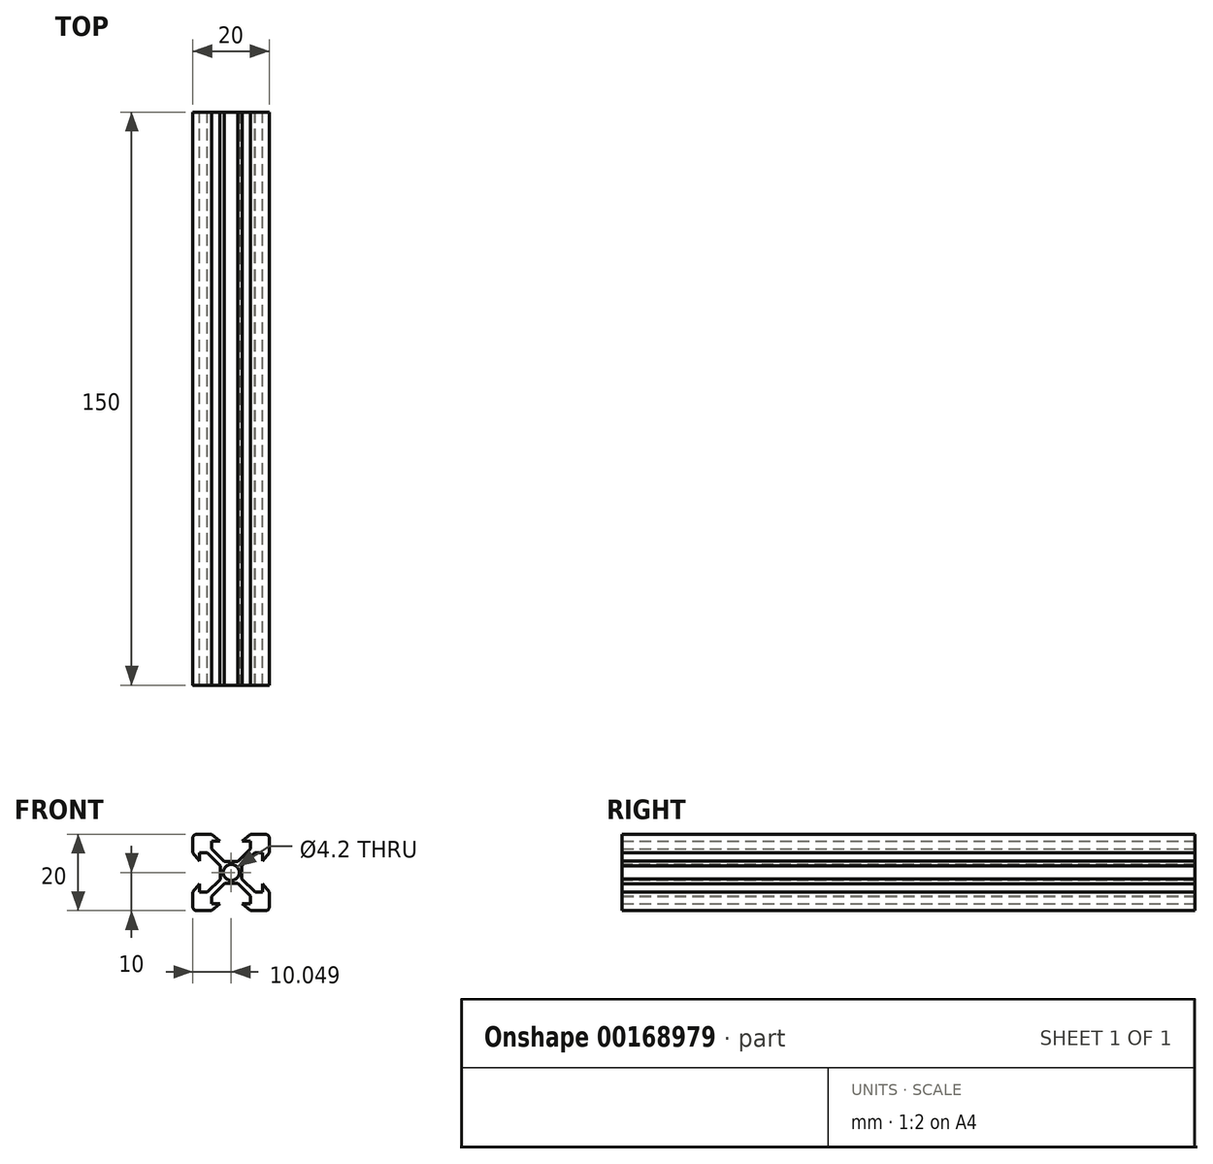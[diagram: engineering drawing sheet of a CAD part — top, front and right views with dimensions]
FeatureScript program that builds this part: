
annotation { "Feature Type Name" : "Feature", "Feature Type Description" : "" }
export const myFeature = defineFeature(function(context is Context, id is Id, definition is map)
    precondition{}
    {
        {
            var Q0;
            Q0=qCreatedBy(makeId("Front.planeOp"),FACE);
            var sketch = newSketch(context, id + "F0", { "sketchPlane" : qUnion([Q0])});
            skLineSegment(sketch, "E0.left", {"start": v(15, 1) * mm, "end": v(15, 4.89) * mm});
            skLineSegment(sketch, "E0.right", {"start": v(35, 1) * mm, "end": v(35, 4.89) * mm});
            skLineSegment(sketch, "E1.right", {"start": v(33.2, 2.97) * mm, "end": v(33.2, 7.06) * mm});
            skLineSegment(sketch, "E2.rect.bottom", {"start": v(26.78, 12.84) * mm, "end": v(23.22, 12.84) * mm});
            skLineSegment(sketch, "E2.rect.top", {"start": v(26.78, 7.16) * mm, "end": v(23.31, 7.16) * mm});
            skLineSegment(sketch, "E2.rect.left", {"start": v(27.84, 11.78) * mm, "end": v(27.84, 8.33) * mm});
            skLineSegment(sketch, "E2.rect.right", {"start": v(22.16, 11.78) * mm, "end": v(22.16, 8.22) * mm});
            skLineSegment(sketch, "E3.rect.bottom", {"start": v(35, 15.12) * mm, "end": v(35, 15.12) * mm});
            skLineSegment(sketch, "E4.rect.bottom", {"start": v(33.2, 12.95) * mm, "end": v(33.2, 12.95) * mm});
            skPoint(sketch, "E4.rect.middle", {"position": v(33.2, 10) * mm});
            skLineSegment(sketch, "E5", {"start": v(35, 4.88) * mm, "end": v(33.2, 7.05) * mm});
            skLineSegment(sketch, "E6", {"start": v(28.37, 12.3) * mm, "end": v(33.2, 17.14) * mm});
            skLineSegment(sketch, "E7", {"start": v(27.3, 13.37) * mm, "end": v(32.14, 18.2) * mm});
            skLineSegment(sketch, "E8", {"start": v(22.7, 13.37) * mm, "end": v(17.86, 18.2) * mm});
            skLineSegment(sketch, "E9", {"start": v(28.37, 7.8) * mm, "end": v(33.2, 2.97) * mm});
            skLineSegment(sketch, "E10", {"start": v(22.74, 6.58) * mm, "end": v(17.95, 1.8) * mm});
            skLineSegment(sketch, "E11", {"start": v(27.36, 6.58) * mm, "end": v(32.14, 1.8) * mm});
            skLineSegment(sketch, "E12", {"start": v(21.63, 7.7) * mm, "end": v(16.8, 2.86) * mm});
            skLineSegment(sketch, "E13", {"start": v(22.7, 13.37) * mm, "end": v(23.22, 12.84) * mm});
            skLineSegment(sketch, "E14", {"start": v(27.3, 13.37) * mm, "end": v(26.78, 12.84) * mm});
            skLineSegment(sketch, "E15", {"start": v(28.37, 12.3) * mm, "end": v(27.84, 11.78) * mm});
            skLineSegment(sketch, "E16", {"start": v(28.37, 7.8) * mm, "end": v(27.84, 8.33) * mm});
            skLineSegment(sketch, "E17", {"start": v(27.36, 6.58) * mm, "end": v(26.78, 7.16) * mm});
            skLineSegment(sketch, "E18", {"start": v(22.74, 6.58) * mm, "end": v(23.31, 7.16) * mm});
            skLineSegment(sketch, "E19", {"start": v(21.63, 7.7) * mm, "end": v(22.16, 8.22) * mm});
            skLineSegment(sketch, "E20", {"start": v(21.63, 12.3) * mm, "end": v(16.8, 17.14) * mm});
            skLineSegment(sketch, "E21", {"start": v(21.63, 12.3) * mm, "end": v(22.16, 11.78) * mm});
            skPoint(sketch, "E22.orphan", {"position": v(22.16, 12.84) * mm});
            skPoint(sketch, "E23.orphan", {"position": v(27.84, 12.84) * mm});
            skPoint(sketch, "E24.orphan", {"position": v(27.84, 7.16) * mm});
            skPoint(sketch, "E25.orphan", {"position": v(22.16, 7.16) * mm});
            skPoint(sketch, "E26.orphan", {"position": v(33.2, 18.2) * mm});
            skPoint(sketch, "E27.orphan", {"position": v(33.2, 1.8) * mm});
            skLineSegment(sketch, "E28.trimOffspring", {"start": v(35, 15.12) * mm, "end": v(35, 19) * mm});
            skLineSegment(sketch, "E29.rect.left", {"start": v(28.21, 18.2) * mm, "end": v(28.21, 18.2) * mm});
            skLineSegment(sketch, "E29.rect.right", {"start": v(21.79, 18.2) * mm, "end": v(21.79, 18.2) * mm});
            skLineSegment(sketch, "E30.rect.left", {"start": v(27.72, 16.15) * mm, "end": v(27.72, 16.15) * mm});
            skLineSegment(sketch, "E30.rect.right", {"start": v(21.83, 16.15) * mm, "end": v(21.83, 16.15) * mm});
            skLineSegment(sketch, "E31.trimOffspring", {"start": v(15, 15.12) * mm, "end": v(15, 19) * mm});
            skPoint(sketch, "E32.visualSharp", {"position": v(15, 20) * mm});
            skArc(sketch, "E32.filletArc", {"start": v(16, 20) * mm, "mid": v(15.3, 19.7) * mm, "end": v(15, 19) * mm});
            skArc(sketch, "E33.filletArc", {"start": v(34, 0) * mm, "mid": v(34.7, 0.3) * mm, "end": v(35, 1) * mm});
            skPoint(sketch, "E34.visualSharp", {"position": v(35, 20) * mm});
            skArc(sketch, "E34.filletArc", {"start": v(35, 19) * mm, "mid": v(34.7, 19.7) * mm, "end": v(34, 20) * mm});
            skLineSegment(sketch, "E35", {"start": v(17.95, 1.8) * mm, "end": v(17.95, 0) * mm});
            skArc(sketch, "E36.filletArc", {"start": v(15, 1) * mm, "mid": v(15.3, 0.3) * mm, "end": v(16, 0) * mm});
            skLineSegment(sketch, "E37", {"start": v(16.8, 17.14) * mm, "end": v(17.86, 18.2) * mm});
            skPoint(sketch, "E38.visualSharp", {"position": v(16.8, 12.95) * mm});
            skLineSegment(sketch, "E39", {"start": v(16.8, 2.86) * mm, "end": v(17.95, 1.8) * mm});
            skLineSegment(sketch, "E40", {"start": v(32.14, 1.8) * mm, "end": v(33.2, 2.97) * mm});
            skLineSegment(sketch, "E41", {"start": v(32.14, 18.2) * mm, "end": v(33.2, 17.14) * mm});
            skLineSegment(sketch, "E42", {"start": v(33.2, 17.14) * mm, "end": v(33.2, 12.94) * mm});
            skLineSegment(sketch, "E43", {"start": v(35, 15.12) * mm, "end": v(33.2, 12.95) * mm});
            skPoint(sketch, "E44.visualSharp", {"position": v(16.8, 7.06) * mm});
            skLineSegment(sketch, "E45", {"start": v(33.2, 15.12) * mm, "end": v(31.18, 15.12) * mm});
            skLineSegment(sketch, "E46", {"start": v(16.8, 15.12) * mm, "end": v(18.82, 15.12) * mm});
            skLineSegment(sketch, "E47", {"start": v(16.8, 4.89) * mm, "end": v(18.82, 4.89) * mm});
            skLineSegment(sketch, "E48", {"start": v(33.2, 4.89) * mm, "end": v(31.28, 4.88) * mm});
            skLineSegment(sketch, "E49.rect.left", {"start": v(26.7, 18.2) * mm, "end": v(26.7, 18.2) * mm});
            skLineSegment(sketch, "E49.rect.right", {"start": v(23.3, 18.2) * mm, "end": v(23.3, 18.2) * mm});
            skPoint(sketch, "E49.rect.middle", {"position": v(25, 18.2) * mm});
            skLineSegment(sketch, "E50.rect.left", {"start": v(30.11, 20) * mm, "end": v(30.11, 20) * mm});
            skLineSegment(sketch, "E50.rect.right", {"start": v(19.88, 20) * mm, "end": v(19.88, 20) * mm});
            skPoint(sketch, "E50.rect.middle", {"position": v(25, 20) * mm});
            skLineSegment(sketch, "E51.rect.left", {"start": v(27.95, 18.2) * mm, "end": v(27.95, 18.2) * mm});
            skLineSegment(sketch, "E51.rect.right", {"start": v(22.05, 18.2) * mm, "end": v(22.05, 18.2) * mm});
            skLineSegment(sketch, "E52", {"start": v(22.05, 18.2) * mm, "end": v(19.88, 20) * mm});
            skLineSegment(sketch, "E53", {"start": v(27.94, 18.2) * mm, "end": v(30.11, 20) * mm});
            skLineSegment(sketch, "E54", {"start": v(27.94, 18.2) * mm, "end": v(32.14, 18.2) * mm});
            skLineSegment(sketch, "E55", {"start": v(30.11, 20) * mm, "end": v(34, 20) * mm});
            skLineSegment(sketch, "E56", {"start": v(19.88, 20) * mm, "end": v(16, 20) * mm});
            skLineSegment(sketch, "E57", {"start": v(17.86, 18.2) * mm, "end": v(22.05, 18.2) * mm});
            skLineSegment(sketch, "E58", {"start": v(15, 15.11) * mm, "end": v(16.8, 12.94) * mm});
            skLineSegment(sketch, "E59", {"start": v(16.8, 17.14) * mm, "end": v(16.8, 12.95) * mm});
            skLineSegment(sketch, "E60", {"start": v(15, 4.89) * mm, "end": v(16.8, 7.06) * mm});
            skLineSegment(sketch, "E61", {"start": v(16.8, 2.86) * mm, "end": v(16.8, 7.06) * mm});
            skLineSegment(sketch, "E62", {"start": v(22.05, 1.8) * mm, "end": v(19.88, 0) * mm});
            skLineSegment(sketch, "E63", {"start": v(27.94, 1.8) * mm, "end": v(30.11, 0) * mm});
            skLineSegment(sketch, "E64", {"start": v(16, 0) * mm, "end": v(19.88, 0) * mm});
            skLineSegment(sketch, "E65", {"start": v(30.11, 0) * mm, "end": v(34, 0) * mm});
            skLineSegment(sketch, "E66", {"start": v(27.94, 1.8) * mm, "end": v(32.14, 1.8) * mm});
            skLineSegment(sketch, "E67", {"start": v(22.05, 1.8) * mm, "end": v(17.95, 1.8) * mm});
            skLineSegment(sketch, "E68", {"start": v(19.88, 1.8) * mm, "end": v(19.88, 3.73) * mm});
            skLineSegment(sketch, "E69", {"start": v(30.11, 1.8) * mm, "end": v(30.11, 3.83) * mm});
            skLineSegment(sketch, "E70", {"start": v(30.11, 18.2) * mm, "end": v(30.11, 16.18) * mm});
            skLineSegment(sketch, "E71", {"start": v(19.88, 16.18) * mm, "end": v(19.88, 18.2) * mm});
            skLineSegment(sketch, "E72", {"start": v(15, 0) * mm, "end": v(-35, 0) * mm});
            skLineSegment(sketch, "E73", {"start": v(35, 0) * mm, "end": v(35, 20) * mm});
            skLineSegment(sketch, "E74", {"start": v(34, 0) * mm, "end": v(35, 0) * mm});
            skLineSegment(sketch, "E75", {"start": v(34, 20) * mm, "end": v(35, 20) * mm});
            skLineSegment(sketch, "E76.0.MirrorCS", {"start": v(36, 0) * mm, "end": v(35, 0) * mm});
            skArc(sketch, "E76.1.MirrorCS", {"start": v(36, 0) * mm, "mid": v(35.3, 0.3) * mm, "end": v(35, 1) * mm});
            skLineSegment(sketch, "E76.2.MirrorCS", {"start": v(36, 20) * mm, "end": v(35, 20) * mm});
            skLineSegment(sketch, "E76.3.MirrorCS", {"start": v(54, 0) * mm, "end": v(50.12, 0) * mm});
            skLineSegment(sketch, "E76.4.MirrorCS", {"start": v(48.37, 7.7) * mm, "end": v(47.84, 8.22) * mm});
            skArc(sketch, "E76.5.MirrorCS", {"start": v(35, 19) * mm, "mid": v(35.3, 19.7) * mm, "end": v(36, 20) * mm});
            skLineSegment(sketch, "E76.6.MirrorCS", {"start": v(37.86, 1.8) * mm, "end": v(36.8, 2.97) * mm});
            skArc(sketch, "E76.7.MirrorCS", {"start": v(54, 20) * mm, "mid": v(54.7, 19.7) * mm, "end": v(55, 19) * mm});
            skLineSegment(sketch, "E76.8.MirrorCS", {"start": v(42.64, 6.58) * mm, "end": v(43.22, 7.16) * mm});
            skLineSegment(sketch, "E76.9.MirrorCS", {"start": v(41.63, 7.8) * mm, "end": v(42.16, 8.33) * mm});
            skLineSegment(sketch, "E76.10.MirrorCS", {"start": v(37.86, 18.2) * mm, "end": v(36.8, 17.14) * mm});
            skLineSegment(sketch, "E76.11.MirrorCS", {"start": v(42.7, 13.37) * mm, "end": v(43.22, 12.84) * mm});
            skLineSegment(sketch, "E76.12.MirrorCS", {"start": v(53.2, 2.86) * mm, "end": v(52.05, 1.8) * mm});
            skLineSegment(sketch, "E76.13.MirrorCS", {"start": v(53.2, 17.14) * mm, "end": v(52.14, 18.2) * mm});
            skLineSegment(sketch, "E76.14.MirrorCS", {"start": v(48.37, 12.3) * mm, "end": v(47.84, 11.78) * mm});
            skLineSegment(sketch, "E76.15.MirrorCS", {"start": v(47.3, 13.37) * mm, "end": v(46.78, 12.84) * mm});
            skLineSegment(sketch, "E76.16.MirrorCS", {"start": v(47.26, 6.58) * mm, "end": v(46.69, 7.16) * mm});
            skLineSegment(sketch, "E76.17.MirrorCS", {"start": v(36.8, 15.12) * mm, "end": v(38.82, 15.12) * mm});
            skLineSegment(sketch, "E76.19.MirrorCS", {"start": v(54, 0) * mm, "end": v(50.12, 0) * mm});
            skLineSegment(sketch, "E76.20.MirrorCS", {"start": v(36.8, 4.89) * mm, "end": v(38.72, 4.88) * mm});
            skArc(sketch, "E76.21.MirrorCS", {"start": v(55, 1) * mm, "mid": v(54.7, 0.3) * mm, "end": v(54, 0) * mm});
            skLineSegment(sketch, "E76.22.MirrorCS", {"start": v(55, 4.89) * mm, "end": v(53.2, 7.06) * mm});
            skLineSegment(sketch, "E76.23.MirrorCS", {"start": v(52.14, 18.2) * mm, "end": v(47.95, 18.2) * mm});
            skLineSegment(sketch, "E76.25.MirrorCS", {"start": v(47.95, 18.2) * mm, "end": v(50.12, 20) * mm});
            skLineSegment(sketch, "E76.26.MirrorCS", {"start": v(50.12, 1.8) * mm, "end": v(50.12, 3.73) * mm});
            skLineSegment(sketch, "E76.27.MirrorCS", {"start": v(39.89, 0) * mm, "end": v(36, 0) * mm});
            skLineSegment(sketch, "E76.28.MirrorCS", {"start": v(53.2, 15.12) * mm, "end": v(51.18, 15.12) * mm});
            skPoint(sketch, "E76.29.MirrorP", {"position": v(45, 18.2) * mm});
            skLineSegment(sketch, "E76.30.MirrorCS", {"start": v(48.21, 18.2) * mm, "end": v(48.21, 18.2) * mm});
            skLineSegment(sketch, "E76.31.MirrorCS", {"start": v(42.06, 18.2) * mm, "end": v(39.89, 20) * mm});
            skLineSegment(sketch, "E76.32.MirrorCS", {"start": v(41.63, 12.3) * mm, "end": v(42.16, 11.78) * mm});
            skLineSegment(sketch, "E76.33.MirrorCS", {"start": v(41.79, 18.2) * mm, "end": v(41.79, 18.2) * mm});
            skLineSegment(sketch, "E76.34.MirrorCS", {"start": v(36.8, 17.14) * mm, "end": v(36.8, 12.94) * mm});
            skLineSegment(sketch, "E76.35.MirrorCS", {"start": v(50.12, 16.18) * mm, "end": v(50.12, 18.2) * mm});
            skLineSegment(sketch, "E76.36.MirrorCS", {"start": v(42.06, 1.8) * mm, "end": v(39.89, 0) * mm});
            skLineSegment(sketch, "E76.37.MirrorCS", {"start": v(35, 15.12) * mm, "end": v(36.8, 12.95) * mm});
            skLineSegment(sketch, "E76.38.MirrorCS", {"start": v(35, 4.88) * mm, "end": v(36.8, 7.05) * mm});
            skLineSegment(sketch, "E76.39.MirrorCS", {"start": v(53.2, 17.14) * mm, "end": v(53.2, 12.95) * mm});
            skLineSegment(sketch, "E76.40.MirrorCS", {"start": v(55, 15.12) * mm, "end": v(53.2, 12.94) * mm});
            skLineSegment(sketch, "E76.41.MirrorCS", {"start": v(53.2, 4.89) * mm, "end": v(51.18, 4.89) * mm});
            skLineSegment(sketch, "E76.42.MirrorCS", {"start": v(36.8, 2.97) * mm, "end": v(36.8, 7.06) * mm});
            skLineSegment(sketch, "E76.43.MirrorCS", {"start": v(39.89, 18.2) * mm, "end": v(39.89, 16.18) * mm});
            skLineSegment(sketch, "E76.44.MirrorCS", {"start": v(42.06, 18.2) * mm, "end": v(37.86, 18.2) * mm});
            skLineSegment(sketch, "E76.45.MirrorCS", {"start": v(53.2, 2.86) * mm, "end": v(53.2, 7.06) * mm});
            skLineSegment(sketch, "E76.46.MirrorCS", {"start": v(42.06, 1.8) * mm, "end": v(37.86, 1.8) * mm});
            skLineSegment(sketch, "E76.47.MirrorCS", {"start": v(52.05, 1.8) * mm, "end": v(52.05, 0) * mm});
            skLineSegment(sketch, "E76.48.MirrorCS", {"start": v(39.89, 1.8) * mm, "end": v(39.89, 3.83) * mm});
            skPoint(sketch, "E76.49.MirrorP", {"position": v(55, 20) * mm});
            skLineSegment(sketch, "E76.50.MirrorCS", {"start": v(47.95, 1.8) * mm, "end": v(52.05, 1.8) * mm});
            skLineSegment(sketch, "E76.51.MirrorCS", {"start": v(41.63, 7.8) * mm, "end": v(36.8, 2.97) * mm});
            skPoint(sketch, "E76.52.MirrorP", {"position": v(53.2, 7.06) * mm});
            skLineSegment(sketch, "E76.53.MirrorCS", {"start": v(43.22, 7.16) * mm, "end": v(46.69, 7.16) * mm});
            skLineSegment(sketch, "E76.54.MirrorCS", {"start": v(55, 1) * mm, "end": v(55, 4.89) * mm});
            skLineSegment(sketch, "E76.55.MirrorCS", {"start": v(55, 15.12) * mm, "end": v(55, 19) * mm});
            skLineSegment(sketch, "E76.56.MirrorCS", {"start": v(48.37, 12.3) * mm, "end": v(53.2, 17.14) * mm});
            skLineSegment(sketch, "E76.57.MirrorCS", {"start": v(42.28, 16.15) * mm, "end": v(42.28, 16.15) * mm});
            skLineSegment(sketch, "E76.58.MirrorCS", {"start": v(36.8, 12.95) * mm, "end": v(36.8, 12.95) * mm});
            skLineSegment(sketch, "E76.60.MirrorCS", {"start": v(42.05, 18.2) * mm, "end": v(42.05, 18.2) * mm});
            skLineSegment(sketch, "E76.61.MirrorCS", {"start": v(47.26, 6.58) * mm, "end": v(52.05, 1.8) * mm});
            skLineSegment(sketch, "E76.62.MirrorCS", {"start": v(42.7, 13.37) * mm, "end": v(37.86, 18.2) * mm});
            skPoint(sketch, "E76.63.MirrorP", {"position": v(42.16, 12.84) * mm});
            skLineSegment(sketch, "E76.64.MirrorCS", {"start": v(48.17, 16.15) * mm, "end": v(48.17, 16.15) * mm});
            skLineSegment(sketch, "E76.65.MirrorCS", {"start": v(42.16, 11.78) * mm, "end": v(42.16, 8.33) * mm});
            skLineSegment(sketch, "E76.66.MirrorCS", {"start": v(47.84, 11.78) * mm, "end": v(47.84, 8.22) * mm});
            skLineSegment(sketch, "E76.67.MirrorCS", {"start": v(43.22, 12.84) * mm, "end": v(46.78, 12.84) * mm});
            skPoint(sketch, "E76.68.MirrorP", {"position": v(36.8, 18.2) * mm});
            skPoint(sketch, "E76.69.MirrorP", {"position": v(53.2, 12.95) * mm});
            skLineSegment(sketch, "E76.72.MirrorCS", {"start": v(39.89, 20) * mm, "end": v(36, 20) * mm});
            skPoint(sketch, "E76.73.MirrorP", {"position": v(42.16, 7.16) * mm});
            skLineSegment(sketch, "E76.74.MirrorCS", {"start": v(47.3, 13.37) * mm, "end": v(52.14, 18.2) * mm});
            skLineSegment(sketch, "E76.75.MirrorCS", {"start": v(43.3, 18.2) * mm, "end": v(43.3, 18.2) * mm});
            skLineSegment(sketch, "E76.76.MirrorCS", {"start": v(39.89, 0) * mm, "end": v(36, 0) * mm});
            skLineSegment(sketch, "E76.77.MirrorCS", {"start": v(54, 0) * mm, "end": v(50.12, 0) * mm});
            skLineSegment(sketch, "E76.78.MirrorCS", {"start": v(39.89, 0) * mm, "end": v(36, 0) * mm});
            skPoint(sketch, "E76.79.MirrorP", {"position": v(45, 20) * mm});
            skPoint(sketch, "E76.80.MirrorP", {"position": v(47.84, 7.16) * mm});
            skLineSegment(sketch, "E76.81.MirrorCS", {"start": v(39.89, 20) * mm, "end": v(39.89, 20) * mm});
            skLineSegment(sketch, "E76.82.MirrorCS", {"start": v(47.95, 18.2) * mm, "end": v(47.95, 18.2) * mm});
            skLineSegment(sketch, "E76.83.MirrorCS", {"start": v(50.12, 20) * mm, "end": v(50.12, 20) * mm});
            skLineSegment(sketch, "E76.84.MirrorCS", {"start": v(41.63, 12.3) * mm, "end": v(36.8, 17.14) * mm});
            skLineSegment(sketch, "E76.85.MirrorCS", {"start": v(48.37, 7.7) * mm, "end": v(53.2, 2.86) * mm});
            skPoint(sketch, "E76.86.MirrorP", {"position": v(36.8, 1.8) * mm});
            skPoint(sketch, "E76.87.MirrorP", {"position": v(36.8, 10) * mm});
            skPoint(sketch, "E76.88.MirrorP", {"position": v(45, 18.2) * mm});
            skPoint(sketch, "E76.89.MirrorP", {"position": v(47.84, 12.84) * mm});
            skLineSegment(sketch, "E76.90.MirrorCS", {"start": v(47.95, 1.8) * mm, "end": v(50.12, 0) * mm});
            skLineSegment(sketch, "E76.91.MirrorCS", {"start": v(42.64, 6.58) * mm, "end": v(37.86, 1.8) * mm});
            skLineSegment(sketch, "E76.94.MirrorCS", {"start": v(50.12, 20) * mm, "end": v(54, 20) * mm});
            skLineSegment(sketch, "E76.95.MirrorCS", {"start": v(46.7, 18.2) * mm, "end": v(46.7, 18.2) * mm});
            skSolve(sketch);
        }
        {
            var Q0;
            Q0=makeQuery(id+"F0.imprint","IMPRINT",FACE,{"disambiguationData":[TD([[makeQuery(id+"F0.imprint","IMPRINT",EDGE,{"derivedFrom":sQuery(id+"F0.wireOp",EDGE,"E2.rect.bottom")}),1.0]])]});
            var Q1;
            {var subQ3=sQuery(id+"F0.wireOp",EDGE,"E69");Q1=makeQuery(id+"F0.imprint","IMPRINT",FACE,{"disambiguationData":[TD([[makeQuery(id+"F0.imprint","IMPRINT",EDGE,{"derivedFrom":subQ3}),-1.0]])]});}
            var Q2;
            {var subQ3=sQuery(id+"F0.wireOp",EDGE,"E47");Q2=makeQuery(id+"F0.imprint","IMPRINT",FACE,{"disambiguationData":[TD([[makeQuery(id+"F0.imprint","IMPRINT",EDGE,{"derivedFrom":subQ3}),-1.0]])]});}
            var Q3;
            Q3=makeQuery(id+"F0.imprint","IMPRINT",FACE,{"disambiguationData":[TD([[makeQuery(id+"F0.imprint","IMPRINT",EDGE,{"derivedFrom":sQuery(id+"F0.wireOp",EDGE,"E0.left")}),-1.0]])]});
            var Q4;
            {var subQ1=sQuery(id+"F0.wireOp",EDGE,"E35");Q4=makeQuery(id+"F0.imprint","IMPRINT",FACE,{"disambiguationData":[TD([[makeQuery(id+"F0.imprint","IMPRINT",EDGE,{"derivedFrom":subQ1}),1.0]])]});}
            var Q5;
            Q5=makeQuery(id+"F0.imprint","IMPRINT",FACE,{"disambiguationData":[TD([[makeQuery(id+"F0.imprint","IMPRINT",EDGE,{"derivedFrom":sQuery(id+"F0.wireOp",EDGE,"E31.trimOffspring")}),-1.0]])]});
            var Q6;
            {var subQ3=sQuery(id+"F0.wireOp",EDGE,"E71");Q6=makeQuery(id+"F0.imprint","IMPRINT",FACE,{"disambiguationData":[TD([[makeQuery(id+"F0.imprint","IMPRINT",EDGE,{"derivedFrom":subQ3}),1.0]])]});}
            var Q7;
            Q7=makeQuery(id+"F0.imprint","IMPRINT",FACE,{"disambiguationData":[TD([[makeQuery(id+"F0.imprint","IMPRINT",EDGE,{"derivedFrom":sQuery(id+"F0.wireOp",EDGE,"E34.filletArc")}),1.0]])]});
            var Q8;
            {var subQ3=sQuery(id+"F0.wireOp",EDGE,"E45");Q8=makeQuery(id+"F0.imprint","IMPRINT",FACE,{"disambiguationData":[TD([[makeQuery(id+"F0.imprint","IMPRINT",EDGE,{"derivedFrom":subQ3}),-1.0]])]});}
            var Q9;
            {var subQ3=sQuery(id+"F0.wireOp",EDGE,"E48");Q9=makeQuery(id+"F0.imprint","IMPRINT",FACE,{"disambiguationData":[TD([[makeQuery(id+"F0.imprint","IMPRINT",EDGE,{"derivedFrom":subQ3}),1.0]])]});}
            var Q10;
            {var subQ3=sQuery(id+"F0.wireOp",EDGE,"E5");Q10=makeQuery(id+"F0.imprint","IMPRINT",FACE,{"disambiguationData":[TD([[makeQuery(id+"F0.imprint","IMPRINT",EDGE,{"derivedFrom":subQ3}),1.0]])]});}
            var Q11;
            {var subQ3=sQuery(id+"F0.wireOp",EDGE,"E68");Q11=makeQuery(id+"F0.imprint","IMPRINT",FACE,{"disambiguationData":[TD([[makeQuery(id+"F0.imprint","IMPRINT",EDGE,{"derivedFrom":subQ3}),1.0]])]});}
            var Q12;
            {var subQ3=sQuery(id+"F0.wireOp",EDGE,"E46");Q12=makeQuery(id+"F0.imprint","IMPRINT",FACE,{"disambiguationData":[TD([[makeQuery(id+"F0.imprint","IMPRINT",EDGE,{"derivedFrom":subQ3}),1.0]])]});}
            var Q13;
            {var subQ3=sQuery(id+"F0.wireOp",EDGE,"E70");Q13=makeQuery(id+"F0.imprint","IMPRINT",FACE,{"disambiguationData":[TD([[makeQuery(id+"F0.imprint","IMPRINT",EDGE,{"derivedFrom":subQ3}),1.0]])]});}
            extrude(context, id + "F2", {"entities" : qUnion([Q0, Q1, Q2, Q3, Q4, Q5, Q6, Q7, Q8, Q9, Q10, Q11, Q12, Q13]), "depth" : 150 * mm});
        }
        {
            var Q0;
            Q0=makeQuery(id+"F2.opExtrude","CAP_FACE",FACE,{"disambiguationData":[OSD([sQuery(id+"F0.wireOp",EDGE,"E0.left"),sQuery(id+"F0.wireOp",EDGE,"E1.right"),sQuery(id+"F0.wireOp",EDGE,"E2.rect.bottom"),sQuery(id+"F0.wireOp",EDGE,"E2.rect.top"),sQuery(id+"F0.wireOp",EDGE,"E2.rect.left"),sQuery(id+"F0.wireOp",EDGE,"E2.rect.right"),sQuery(id+"F0.wireOp",EDGE,"E5"),sQuery(id+"F0.wireOp",EDGE,"E6"),sQuery(id+"F0.wireOp",EDGE,"E7"),sQuery(id+"F0.wireOp",EDGE,"E8"),sQuery(id+"F0.wireOp",EDGE,"E9"),sQuery(id+"F0.wireOp",EDGE,"E10"),sQuery(id+"F0.wireOp",EDGE,"E11"),sQuery(id+"F0.wireOp",EDGE,"E12"),sQuery(id+"F0.wireOp",EDGE,"E13"),sQuery(id+"F0.wireOp",EDGE,"E14"),sQuery(id+"F0.wireOp",EDGE,"E15"),sQuery(id+"F0.wireOp",EDGE,"E16"),sQuery(id+"F0.wireOp",EDGE,"E17"),sQuery(id+"F0.wireOp",EDGE,"E18"),sQuery(id+"F0.wireOp",EDGE,"E19"),sQuery(id+"F0.wireOp",EDGE,"E20"),sQuery(id+"F0.wireOp",EDGE,"E21"),sQuery(id+"F0.wireOp",EDGE,"E31.trimOffspring"),sQuery(id+"F0.wireOp",EDGE,"E32.filletArc"),sQuery(id+"F0.wireOp",EDGE,"E33.filletArc"),sQuery(id+"F0.wireOp",EDGE,"E34.filletArc"),sQuery(id+"F0.wireOp",EDGE,"E36.filletArc"),sQuery(id+"F0.wireOp",EDGE,"E42"),sQuery(id+"F0.wireOp",EDGE,"E43"),sQuery(id+"F0.wireOp",EDGE,"E45"),sQuery(id+"F0.wireOp",EDGE,"E46"),sQuery(id+"F0.wireOp",EDGE,"E47"),sQuery(id+"F0.wireOp",EDGE,"E48"),sQuery(id+"F0.wireOp",EDGE,"E52"),sQuery(id+"F0.wireOp",EDGE,"E53"),sQuery(id+"F0.wireOp",EDGE,"E54"),sQuery(id+"F0.wireOp",EDGE,"E55"),sQuery(id+"F0.wireOp",EDGE,"E56"),sQuery(id+"F0.wireOp",EDGE,"E57"),sQuery(id+"F0.wireOp",EDGE,"E58"),sQuery(id+"F0.wireOp",EDGE,"E59"),sQuery(id+"F0.wireOp",EDGE,"E60"),sQuery(id+"F0.wireOp",EDGE,"E61"),sQuery(id+"F0.wireOp",EDGE,"E62"),sQuery(id+"F0.wireOp",EDGE,"E63"),sQuery(id+"F0.wireOp",EDGE,"E66"),sQuery(id+"F0.wireOp",EDGE,"E67"),sQuery(id+"F0.wireOp",EDGE,"E68"),sQuery(id+"F0.wireOp",EDGE,"E69"),sQuery(id+"F0.wireOp",EDGE,"E70"),sQuery(id+"F0.wireOp",EDGE,"E71"),sQuery(id+"F0.wireOp",EDGE,"E64"),sQuery(id+"F0.wireOp",EDGE,"E65"),sQuery(id+"F0.wireOp",EDGE,"E28.trimOffspring"),sQuery(id+"F0.wireOp",EDGE,"E0.right")])],"isStart":false});
            var sketch = newSketch(context, id + "F1", { "sketchPlane" : qUnion([Q0])});
            skPoint(sketch, "E77", {"position": v(25.05, 10) * mm});
            skPoint(sketch, "E77.positionSnap0", {"position": v(22.16, 10) * mm});
            skPoint(sketch, "E77.positionSnap1", {"position": v(25.05, 7.16) * mm});
            skSolve(sketch);
        }
        {
            var Q0;
            Q0=sQuery(id+"F1.wireOp",VERTEX,"E77");
            var Q1;
            Q1=makeQuery(id+"F2.opExtrude","SWEPT_BODY",BODY,{"disambiguationData":[OSD([sQuery(id+"F0.wireOp",EDGE,"E0.left"),sQuery(id+"F0.wireOp",EDGE,"E1.right"),sQuery(id+"F0.wireOp",EDGE,"E2.rect.bottom"),sQuery(id+"F0.wireOp",EDGE,"E2.rect.top"),sQuery(id+"F0.wireOp",EDGE,"E2.rect.left"),sQuery(id+"F0.wireOp",EDGE,"E2.rect.right"),sQuery(id+"F0.wireOp",EDGE,"E5"),sQuery(id+"F0.wireOp",EDGE,"E6"),sQuery(id+"F0.wireOp",EDGE,"E7"),sQuery(id+"F0.wireOp",EDGE,"E8"),sQuery(id+"F0.wireOp",EDGE,"E9"),sQuery(id+"F0.wireOp",EDGE,"E10"),sQuery(id+"F0.wireOp",EDGE,"E11"),sQuery(id+"F0.wireOp",EDGE,"E12"),sQuery(id+"F0.wireOp",EDGE,"E13"),sQuery(id+"F0.wireOp",EDGE,"E14"),sQuery(id+"F0.wireOp",EDGE,"E15"),sQuery(id+"F0.wireOp",EDGE,"E16"),sQuery(id+"F0.wireOp",EDGE,"E17"),sQuery(id+"F0.wireOp",EDGE,"E18"),sQuery(id+"F0.wireOp",EDGE,"E19"),sQuery(id+"F0.wireOp",EDGE,"E20"),sQuery(id+"F0.wireOp",EDGE,"E21"),sQuery(id+"F0.wireOp",EDGE,"E31.trimOffspring"),sQuery(id+"F0.wireOp",EDGE,"E32.filletArc"),sQuery(id+"F0.wireOp",EDGE,"E33.filletArc"),sQuery(id+"F0.wireOp",EDGE,"E34.filletArc"),sQuery(id+"F0.wireOp",EDGE,"E36.filletArc"),sQuery(id+"F0.wireOp",EDGE,"E42"),sQuery(id+"F0.wireOp",EDGE,"E43"),sQuery(id+"F0.wireOp",EDGE,"E45"),sQuery(id+"F0.wireOp",EDGE,"E46"),sQuery(id+"F0.wireOp",EDGE,"E47"),sQuery(id+"F0.wireOp",EDGE,"E48"),sQuery(id+"F0.wireOp",EDGE,"E52"),sQuery(id+"F0.wireOp",EDGE,"E53"),sQuery(id+"F0.wireOp",EDGE,"E54"),sQuery(id+"F0.wireOp",EDGE,"E55"),sQuery(id+"F0.wireOp",EDGE,"E56"),sQuery(id+"F0.wireOp",EDGE,"E57"),sQuery(id+"F0.wireOp",EDGE,"E58"),sQuery(id+"F0.wireOp",EDGE,"E59"),sQuery(id+"F0.wireOp",EDGE,"E60"),sQuery(id+"F0.wireOp",EDGE,"E61"),sQuery(id+"F0.wireOp",EDGE,"E62"),sQuery(id+"F0.wireOp",EDGE,"E63"),sQuery(id+"F0.wireOp",EDGE,"E66"),sQuery(id+"F0.wireOp",EDGE,"E67"),sQuery(id+"F0.wireOp",EDGE,"E68"),sQuery(id+"F0.wireOp",EDGE,"E69"),sQuery(id+"F0.wireOp",EDGE,"E70"),sQuery(id+"F0.wireOp",EDGE,"E71"),sQuery(id+"F0.wireOp",EDGE,"E64"),sQuery(id+"F0.wireOp",EDGE,"E65"),sQuery(id+"F0.wireOp",EDGE,"E28.trimOffspring"),sQuery(id+"F0.wireOp",EDGE,"E0.right")])]});
            hole(context, id + "F3", {"style" : HoleStyle.SIMPLE, "endStyle" : HoleEndStyle.THROUGH, "holeDiameter" : 4.2 * mm, "locations" : qUnion([Q0]), "scope" : qUnion([Q1]), "isTappedThrough" : true});
        }
    });
